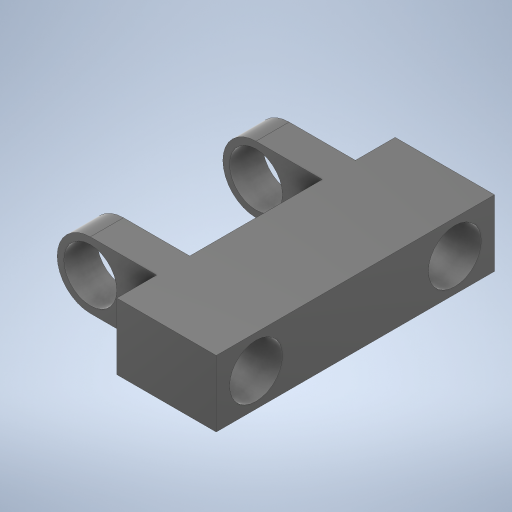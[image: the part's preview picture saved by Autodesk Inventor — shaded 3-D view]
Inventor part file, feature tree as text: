
AUTODESK INVENTOR PART (.ipt)
format: ipt  version: 2023 (Build 270158000, 158)  size: 282,624 bytes
history: native  units: mm
features: extrude x4, sketch x4, fillet x1
ambient origin geometry x8: Origin, YZ Plane, XZ Plane, XY Plane, X Axis, Y Axis, Z Axis, Center Point
bodies: Volumenkörper1 (feature_tree)
feature tree (9):
  extrude  "Extrusion1"  Depth=42.0mm
  extrude  "Extrusion2"  Depth=15.0mm
  extrude  "Extrusion3"  Depth=15.0mm
  fillet  "Rundung1"  Radius=15.0mm
  extrude  "Extrusion4"  Depth=5.0mm
  sketch  "Skizze1"  dims[d0=10.0mm d1=42.0mm]
  sketch  "Skizze2"  dims[d2=15.0mm d3=0.0mm d4=8.0mm]
  sketch  "Skizze3"  dims[d5=8.0mm d6=15.0mm d7=15.0mm]
  sketch  "Skizze4"  dims[d8=10.0mm d9=0.0mm d10=5.0mm d11=5.0mm d12=10.0mm d13=10.0mm d14=15.0mm d15=0.0mm d16=5.0mm d17=8.0mm d18=0.0mm d19=0.0mm d20=0.15mm d21=0.25mm d22=0.375mm d23=14.3117mm d24=0.75mm d25=20.594885mm d26=0.0625mm d27=0.75mm d28=0.375mm]
